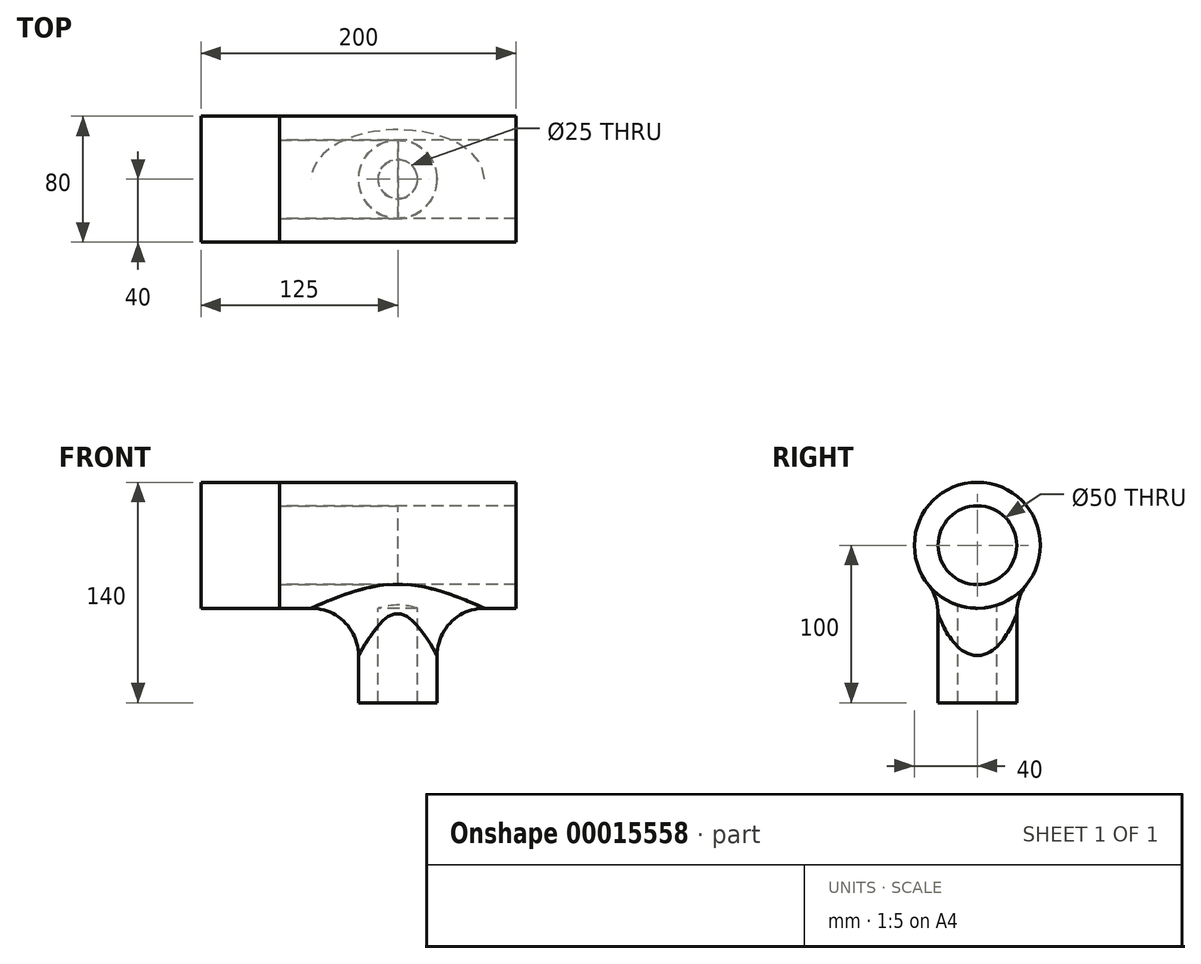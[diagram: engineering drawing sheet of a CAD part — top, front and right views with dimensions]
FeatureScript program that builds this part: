
annotation { "Feature Type Name" : "Feature", "Feature Type Description" : "" }
export const myFeature = defineFeature(function(context is Context, id is Id, definition is map)
    precondition{}
    {
        {
            var Q0;
            Q0=qCreatedBy(makeId("Top.planeOp"),FACE);
            var sketch = newSketch(context, id + "F0", { "sketchPlane" : qUnion([Q0])});
            skCircle(sketch, "E0", {"center": v(0, 0) * mm, "radius": 25 * mm});
            skCircle(sketch, "E1", {"center": v(0, 0) * mm, "radius": 12.5 * mm});
            skSolve(sketch);
        }
        {
            var Q0;
            Q0 = qSketchRegion(id + "F0", true);
            extrude(context, id + "F1", {"entities" : qUnion([Q0]), "oppositeDirection" : true, "depth" : 100 * mm});
        }
        {
            var Q0;
            Q0=qCreatedBy(makeId("Right.planeOp"),FACE);
            var sketch = newSketch(context, id + "F2", { "sketchPlane" : qUnion([Q0])});
            skCircle(sketch, "E2", {"center": v(0, 0) * mm, "radius": 25 * mm});
            skCircle(sketch, "E3", {"center": v(0, 0) * mm, "radius": 40 * mm});
            skLineSegment(sketch, "E4", {"start": v(-25, 0) * mm, "end": v(0, 0) * mm, "construction": true});
            skSolve(sketch);
        }
        {
            var Q0;
            Q0 = qSketchRegion(id + "F2", true);
            extrude(context, id + "F3", {"entities" : qUnion([Q0]), "operationType" : NewBodyOperationType.ADD, "endBound" : BoundingType.SYMMETRIC, "depth" : 150 * mm});
        }
        {
            var Q0;
            Q0=qCreatedBy(makeId("Right.planeOp"),FACE);
            var sketch = newSketch(context, id + "F4", { "sketchPlane" : qUnion([Q0])});
            skCircle(sketch, "E5", {"center": v(0, 0) * mm, "radius": 25 * mm});
            skSolve(sketch);
        }
        {
            var Q0;
            Q0 = qSketchRegion(id + "F4", true);
            extrude(context, id + "F5", {"entities" : qUnion([Q0]), "operationType" : NewBodyOperationType.REMOVE, "endBound" : BoundingType.SYMMETRIC, "depth" : 303.9 * mm});
        }
        {
            var Q0;
            Q0=qCreatedBy(makeId("Front.planeOp"),FACE);
            var sketch = newSketch(context, id + "F6", { "sketchPlane" : qUnion([Q0])});
            skLineSegment(sketch, "E6", {"start": v(0, 25) * mm, "end": v(-75, 25) * mm});
            skLineSegment(sketch, "E7", {"start": v(-75, 25) * mm, "end": v(-75, 40) * mm});
            skLineSegment(sketch, "E8", {"start": v(-75, 40) * mm, "end": v(-125, 40) * mm});
            skLineSegment(sketch, "E9", {"start": v(0, 25) * mm, "end": v(0, 0) * mm});
            skLineSegment(sketch, "E10", {"start": v(0, 0) * mm, "end": v(-125, 0) * mm});
            skLineSegment(sketch, "E11", {"start": v(-125, 0) * mm, "end": v(-125, 40) * mm});
            skSolve(sketch);
        }
        {
            var Q0;
            Q0=makeQuery(id+"F6.imprint","IMPRINT",FACE,{"disambiguationData":[TD([[makeQuery(id+"F6.imprint","IMPRINT",EDGE,{"derivedFrom":sQuery(id+"F6.wireOp",EDGE,"E6")}),1.0]])]});
            var Q1;
            Q1=sQuery(id+"F6.wireOp",EDGE,"E10");
            revolve(context, id + "F7", {"entities" : qUnion([Q0]), "axis" : qUnion([Q1]), "revolveType" : RevolveType.FULL});
        }
        {
            var Q0;
            Q0=makeQuery(id+"F3.boolean.opBoolean","INTERSECT",EDGE,{"derivedFrom":[makeQuery(id+"F1.opExtrude","SWEPT_FACE",FACE,{"disambiguationData":[OSD([sQuery(id+"F0.wireOp",EDGE,"E0")])]}),makeQuery(id+"F3.opExtrude","SWEPT_FACE",FACE,{"disambiguationData":[OSD([sQuery(id+"F2.wireOp",EDGE,"E3")])]})]});
            fillet(context, id + "F8", {"entities" : qUnion([Q0]), "radius" : 30 * mm, "tangentPropagation" : true, "allowEdgeOverflow" : false});
        }
    });
